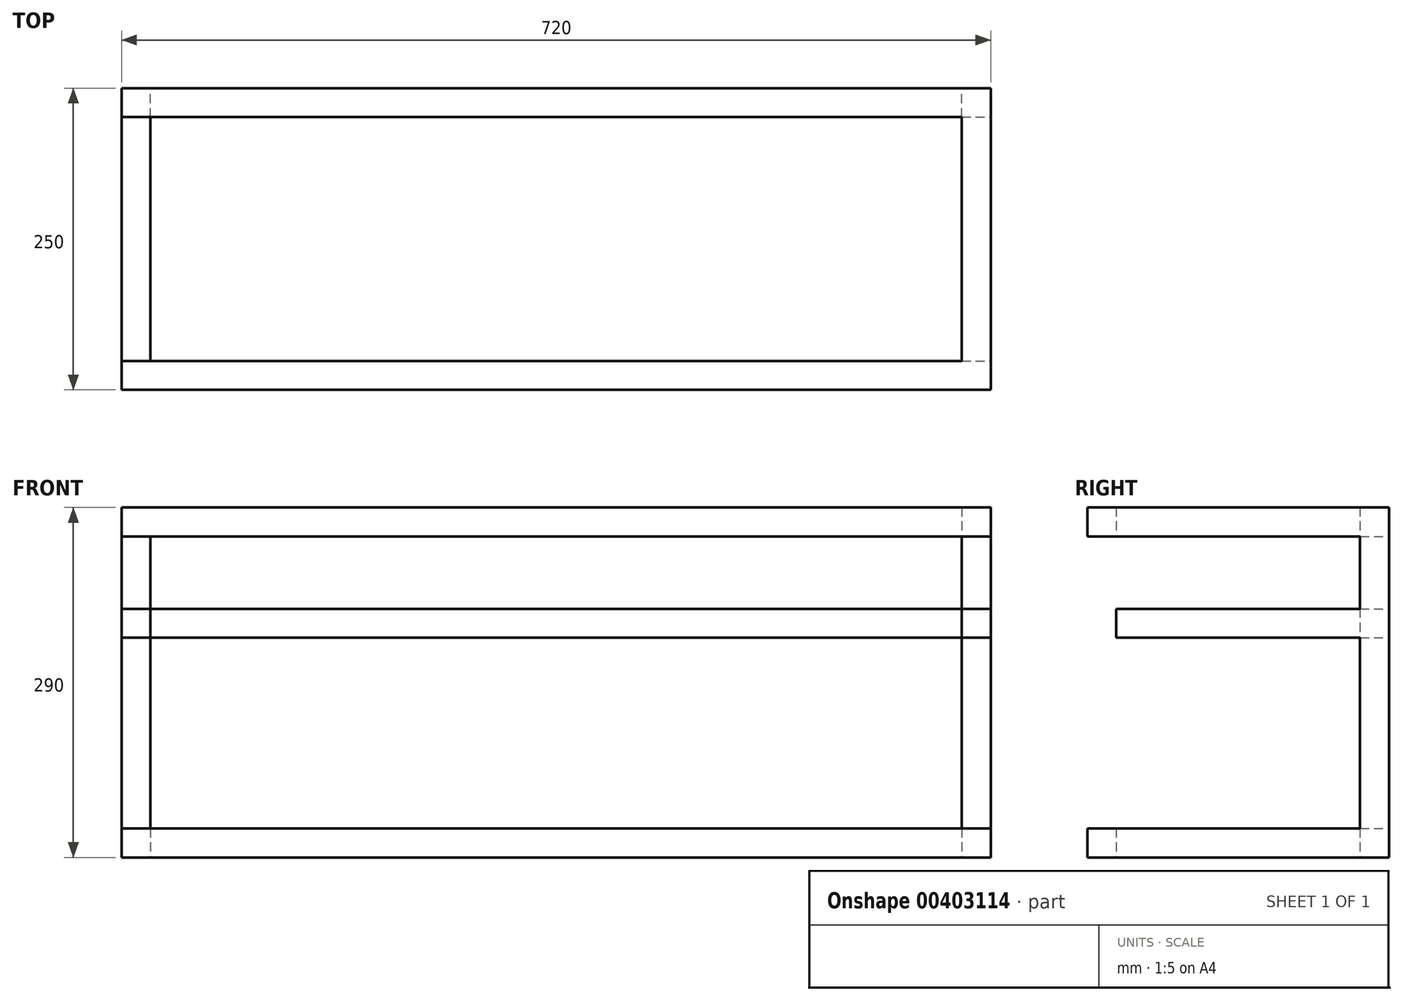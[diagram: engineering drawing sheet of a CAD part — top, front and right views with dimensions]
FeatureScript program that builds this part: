
annotation { "Feature Type Name" : "Feature", "Feature Type Description" : "" }
export const myFeature = defineFeature(function(context is Context, id is Id, definition is map)
    precondition{}
    {
        {
            var Q0;
            Q0=qCreatedBy(makeId("Front.planeOp"),FACE);
            var sketch = newSketch(context, id + "F0", { "sketchPlane" : qUnion([Q0])});
            skLineSegment(sketch, "E0.bottom", {"start": v(-354.03, 182.25) * mm, "end": v(365.97, 182.25) * mm});
            skLineSegment(sketch, "E0.top", {"start": v(-354.03, -107.75) * mm, "end": v(365.97, -107.75) * mm});
            skLineSegment(sketch, "E0.left", {"start": v(-354.03, 182.25) * mm, "end": v(-354.03, -107.75) * mm});
            skLineSegment(sketch, "E0.right", {"start": v(365.97, 182.25) * mm, "end": v(365.97, -107.75) * mm});
            skLineSegment(sketch, "E1", {"start": v(-354.03, -107.75) * mm, "end": v(-354.03, 86.25) * mm});
            skLineSegment(sketch, "E2.top", {"start": v(-354.03, 158.25) * mm, "end": v(365.97, 158.25) * mm});
            skLineSegment(sketch, "E2.left", {"start": v(-354.03, 182.25) * mm, "end": v(-354.03, 158.25) * mm});
            skLineSegment(sketch, "E2.right", {"start": v(365.97, 182.25) * mm, "end": v(365.97, 158.25) * mm});
            skLineSegment(sketch, "E3.bottom", {"start": v(365.97, 158.25) * mm, "end": v(341.97, 158.25) * mm});
            skLineSegment(sketch, "E3.left", {"start": v(365.97, 158.25) * mm, "end": v(365.97, 110.25) * mm});
            skLineSegment(sketch, "E4.bottom", {"start": v(-354.03, 158.25) * mm, "end": v(-330.03, 158.25) * mm});
            skLineSegment(sketch, "E4.left", {"start": v(-354.03, 158.25) * mm, "end": v(-354.03, 110.25) * mm});
            skLineSegment(sketch, "E5.top", {"start": v(-354.03, -83.75) * mm, "end": v(365.97, -83.75) * mm});
            skLineSegment(sketch, "E5.left", {"start": v(-354.03, -107.75) * mm, "end": v(-354.03, -83.75) * mm});
            skLineSegment(sketch, "E5.right", {"start": v(365.97, -107.75) * mm, "end": v(365.97, -83.75) * mm});
            skLineSegment(sketch, "E6.top", {"start": v(-354.03, -83.75) * mm, "end": v(-330.03, -83.75) * mm});
            skLineSegment(sketch, "E6.left", {"start": v(-354.03, 62.25) * mm, "end": v(-354.03, -83.75) * mm});
            skLineSegment(sketch, "E7.top", {"start": v(-354.03, 74.25) * mm, "end": v(365.97, 74.25) * mm});
            skLineSegment(sketch, "E7.right", {"start": v(365.97, 86.25) * mm, "end": v(365.97, 74.25) * mm});
            skLineSegment(sketch, "E8.top", {"start": v(-353.78, 98.25) * mm, "end": v(366.22, 98.25) * mm});
            skLineSegment(sketch, "E8.right", {"start": v(366.22, 86.25) * mm, "end": v(366.22, 98.25) * mm});
            skLineSegment(sketch, "E9.top", {"start": v(-353.78, 98.25) * mm, "end": v(-330.03, 98.25) * mm});
            skLineSegment(sketch, "E9.right", {"start": v(-330.03, 158.25) * mm, "end": v(-330.03, 98.25) * mm});
            skLineSegment(sketch, "E10", {"start": v(341.97, 158.25) * mm, "end": v(341.97, 98.25) * mm});
            skLineSegment(sketch, "E11", {"start": v(-330.03, -83.75) * mm, "end": v(-330.03, 74.25) * mm});
            skLineSegment(sketch, "E12", {"start": v(365.97, -83.75) * mm, "end": v(341.97, -83.75) * mm});
            skLineSegment(sketch, "E13", {"start": v(341.97, -83.75) * mm, "end": v(341.97, 74.25) * mm});
            skLineSegment(sketch, "E14", {"start": v(-354.03, 86.25) * mm, "end": v(365.97, 86.25) * mm});
            skSolve(sketch);
        }
        {
            var Q0;
            {var subQ1=sQuery(id+"F0.wireOp",EDGE,"E4.left");Q0=makeQuery(id+"F0.imprint","IMPRINT",FACE,{"disambiguationData":[TD([[makeQuery(id+"F0.imprint","IMPRINT",EDGE,{"derivedFrom":subQ1}),1.0]])]});}
            var Q1;
            Q1=makeQuery(id+"F0.imprint","IMPRINT",FACE,{"disambiguationData":[TD([[makeQuery(id+"F0.imprint","IMPRINT",EDGE,{"derivedFrom":sQuery(id+"F0.wireOp",EDGE,"E3.bottom")}),1.0]])]});
            var Q2;
            Q2=makeQuery(id+"F0.imprint","IMPRINT",FACE,{"disambiguationData":[TD([[makeQuery(id+"F0.imprint","IMPRINT",EDGE,{"derivedFrom":sQuery(id+"F0.wireOp",EDGE,"E6.top")}),1.0]])]});
            var Q3;
            {var subQ0=sQuery(id+"F0.wireOp",EDGE,"E12");Q3=makeQuery(id+"F0.imprint","IMPRINT",FACE,{"disambiguationData":[TD([[makeQuery(id+"F0.imprint","IMPRINT",EDGE,{"derivedFrom":subQ0}),-1.0]])]});}
            var Q4;
            {var subQ0=sQuery(id+"F0.wireOp",EDGE,"E7.right");Q4=makeQuery(id+"F0.imprint","IMPRINT",FACE,{"disambiguationData":[TD([[makeQuery(id+"F0.imprint","IMPRINT",EDGE,{"derivedFrom":subQ0}),-1.0]])]});}
            var Q5;
            {var subQ0=sQuery(id+"F0.wireOp",EDGE,"E8.right");Q5=makeQuery(id+"F0.imprint","IMPRINT",FACE,{"disambiguationData":[TD([[makeQuery(id+"F0.imprint","IMPRINT",EDGE,{"derivedFrom":subQ0}),1.0]])]});}
            var Q6;
            Q6=makeQuery(id+"F0.imprint","IMPRINT",FACE,{"disambiguationData":[TD([[makeQuery(id+"F0.imprint","IMPRINT",EDGE,{"derivedFrom":sQuery(id+"F0.wireOp",EDGE,"E0.bottom")}),-1.0]])]});
            var Q7;
            Q7=makeQuery(id+"F0.imprint","IMPRINT",FACE,{"disambiguationData":[TD([[makeQuery(id+"F0.imprint","IMPRINT",EDGE,{"derivedFrom":sQuery(id+"F0.wireOp",EDGE,"E0.top")}),1.0]])]});
            extrude(context, id + "F1", {"entities" : qUnion([Q0, Q1, Q2, Q3, Q4, Q5, Q6, Q7]), "oppositeDirection" : true, "depth" : 24 * mm});
        }
        {
            var Q0;
            Q0=makeQuery(id+"F1.opExtrude","CAP_FACE",FACE,{"disambiguationData":[OSD([sQuery(id+"F0.wireOp",EDGE,"E0.left"),sQuery(id+"F0.wireOp",EDGE,"E0.right"),sQuery(id+"F0.wireOp",EDGE,"E1"),sQuery(id+"F0.wireOp",EDGE,"E0.bottom"),sQuery(id+"F0.wireOp",EDGE,"E2.top"),sQuery(id+"F0.wireOp",EDGE,"E2.left"),sQuery(id+"F0.wireOp",EDGE,"E2.right"),sQuery(id+"F0.wireOp",EDGE,"E3.left"),sQuery(id+"F0.wireOp",EDGE,"E4.bottom"),sQuery(id+"F0.wireOp",EDGE,"E4.left"),sQuery(id+"F0.wireOp",EDGE,"E0.top"),sQuery(id+"F0.wireOp",EDGE,"E5.top"),sQuery(id+"F0.wireOp",EDGE,"E5.left"),sQuery(id+"F0.wireOp",EDGE,"E5.right"),sQuery(id+"F0.wireOp",EDGE,"E6.left"),sQuery(id+"F0.wireOp",EDGE,"E7.top"),sQuery(id+"F0.wireOp",EDGE,"E7.right"),sQuery(id+"F0.wireOp",EDGE,"E8.top"),sQuery(id+"F0.wireOp",EDGE,"E8.right"),sQuery(id+"F0.wireOp",EDGE,"E9.right"),sQuery(id+"F0.wireOp",EDGE,"E10"),sQuery(id+"F0.wireOp",EDGE,"E11"),sQuery(id+"F0.wireOp",EDGE,"E13")])],"isStart":false});
            var sketch = newSketch(context, id + "F2", { "sketchPlane" : qUnion([Q0])});
            skLineSegment(sketch, "E15.bottom", {"start": v(-365.97, 182.25) * mm, "end": v(-341.97, 182.25) * mm});
            skLineSegment(sketch, "E15.top", {"start": v(-365.97, 158.25) * mm, "end": v(-341.97, 158.25) * mm});
            skLineSegment(sketch, "E15.left", {"start": v(-365.97, 182.25) * mm, "end": v(-365.97, 158.25) * mm});
            skLineSegment(sketch, "E15.right", {"start": v(-341.97, 182.25) * mm, "end": v(-341.97, 158.25) * mm});
            skLineSegment(sketch, "E16.bottom", {"start": v(-341.97, 98.25) * mm, "end": v(-365.97, 98.25) * mm});
            skLineSegment(sketch, "E16.top", {"start": v(-341.97, 74.25) * mm, "end": v(-365.97, 74.25) * mm});
            skLineSegment(sketch, "E16.left", {"start": v(-341.97, 98.25) * mm, "end": v(-341.97, 74.25) * mm});
            skLineSegment(sketch, "E16.right", {"start": v(-365.97, 98.25) * mm, "end": v(-365.97, 74.25) * mm});
            skLineSegment(sketch, "E17.bottom", {"start": v(-341.97, -83.75) * mm, "end": v(-365.97, -83.75) * mm});
            skLineSegment(sketch, "E17.top", {"start": v(-341.97, -107.75) * mm, "end": v(-365.97, -107.75) * mm});
            skLineSegment(sketch, "E17.left", {"start": v(-341.97, -83.75) * mm, "end": v(-341.97, -107.75) * mm});
            skLineSegment(sketch, "E17.right", {"start": v(-365.97, -83.75) * mm, "end": v(-365.97, -107.75) * mm});
            skLineSegment(sketch, "E18.bottom", {"start": v(330.03, 158.25) * mm, "end": v(354.03, 158.25) * mm});
            skLineSegment(sketch, "E18.top", {"start": v(330.03, 182.25) * mm, "end": v(354.03, 182.25) * mm});
            skLineSegment(sketch, "E18.left", {"start": v(330.03, 158.25) * mm, "end": v(330.03, 182.25) * mm});
            skLineSegment(sketch, "E18.right", {"start": v(354.03, 158.25) * mm, "end": v(354.03, 182.25) * mm});
            skLineSegment(sketch, "E19.bottom", {"start": v(330.03, 98.25) * mm, "end": v(354.03, 98.25) * mm});
            skLineSegment(sketch, "E19.top", {"start": v(330.03, 74.25) * mm, "end": v(354.03, 74.25) * mm});
            skLineSegment(sketch, "E19.left", {"start": v(330.03, 98.25) * mm, "end": v(330.03, 74.25) * mm});
            skLineSegment(sketch, "E19.right", {"start": v(354.03, 98.25) * mm, "end": v(354.03, 74.25) * mm});
            skLineSegment(sketch, "E20.bottom", {"start": v(330.03, -83.75) * mm, "end": v(354.03, -83.75) * mm});
            skLineSegment(sketch, "E20.top", {"start": v(330.03, -107.75) * mm, "end": v(354.03, -107.75) * mm});
            skLineSegment(sketch, "E20.left", {"start": v(330.03, -83.75) * mm, "end": v(330.03, -107.75) * mm});
            skLineSegment(sketch, "E20.right", {"start": v(354.03, -83.75) * mm, "end": v(354.03, -107.75) * mm});
            skSolve(sketch);
        }
        {
            var Q0;
            Q0=makeQuery(id+"F2.imprint","IMPRINT",FACE,{"disambiguationData":[TD([[makeQuery(id+"F2.imprint","IMPRINT",EDGE,{"derivedFrom":sQuery(id+"F2.wireOp",EDGE,"E16.bottom")}),1.0]])]});
            var Q1;
            Q1=makeQuery(id+"F2.imprint","IMPRINT",FACE,{"disambiguationData":[TD([[makeQuery(id+"F2.imprint","IMPRINT",EDGE,{"derivedFrom":sQuery(id+"F2.wireOp",EDGE,"E17.bottom")}),1.0]])]});
            var Q2;
            Q2=makeQuery(id+"F2.imprint","IMPRINT",FACE,{"disambiguationData":[TD([[makeQuery(id+"F2.imprint","IMPRINT",EDGE,{"derivedFrom":sQuery(id+"F2.wireOp",EDGE,"E18.bottom")}),1.0]])]});
            var Q3;
            Q3=makeQuery(id+"F2.imprint","IMPRINT",FACE,{"disambiguationData":[TD([[makeQuery(id+"F2.imprint","IMPRINT",EDGE,{"derivedFrom":sQuery(id+"F2.wireOp",EDGE,"E20.bottom")}),-1.0]])]});
            var Q4;
            Q4=makeQuery(id+"F2.imprint","IMPRINT",FACE,{"disambiguationData":[TD([[makeQuery(id+"F2.imprint","IMPRINT",EDGE,{"derivedFrom":sQuery(id+"F2.wireOp",EDGE,"E19.bottom")}),-1.0]])]});
            var Q5;
            Q5=makeQuery(id+"F2.imprint","IMPRINT",FACE,{"disambiguationData":[TD([[makeQuery(id+"F2.imprint","IMPRINT",EDGE,{"derivedFrom":sQuery(id+"F2.wireOp",EDGE,"E15.bottom")}),1.0]])]});
            extrude(context, id + "F3", {"entities" : qUnion([Q0, Q1, Q2, Q3, Q4, Q5]), "operationType" : NewBodyOperationType.ADD, "depth" : 202 * mm});
        }
        {
            var Q0;
            Q0=makeQuery(id+"F3.boolean.opBoolean","MERGE",FACE,{"derivedFrom":[makeQuery(id+"F1.opExtrude","SWEPT_FACE",FACE,{"disambiguationData":[OSD([sQuery(id+"F0.wireOp",EDGE,"E0.right"),sQuery(id+"F0.wireOp",EDGE,"E2.right"),sQuery(id+"F0.wireOp",EDGE,"E3.left"),sQuery(id+"F0.wireOp",EDGE,"E5.right"),sQuery(id+"F0.wireOp",EDGE,"E7.right")])]}),makeQuery(id+"F3.opExtrude","SWEPT_FACE",FACE,{"disambiguationData":[OSD([sQuery(id+"F2.wireOp",EDGE,"E15.left")])]}),makeQuery(id+"F3.opExtrude","SWEPT_FACE",FACE,{"disambiguationData":[OSD([sQuery(id+"F2.wireOp",EDGE,"E16.right")])]}),makeQuery(id+"F3.opExtrude","SWEPT_FACE",FACE,{"disambiguationData":[OSD([sQuery(id+"F2.wireOp",EDGE,"E17.right")])]})]});
            var sketch = newSketch(context, id + "F4", { "sketchPlane" : qUnion([Q0])});
            skLineSegment(sketch, "E21.bottom", {"start": v(226, 182.25) * mm, "end": v(250, 182.25) * mm});
            skLineSegment(sketch, "E21.top", {"start": v(226, 158.25) * mm, "end": v(250, 158.25) * mm});
            skLineSegment(sketch, "E21.left", {"start": v(226, 182.25) * mm, "end": v(226, 158.25) * mm});
            skLineSegment(sketch, "E21.right", {"start": v(250, 182.25) * mm, "end": v(250, 158.25) * mm});
            skLineSegment(sketch, "E22.bottom", {"start": v(226, 98.25) * mm, "end": v(250, 98.25) * mm});
            skLineSegment(sketch, "E22.top", {"start": v(226, 74.25) * mm, "end": v(250, 74.25) * mm});
            skLineSegment(sketch, "E22.left", {"start": v(226, 98.25) * mm, "end": v(226, 74.25) * mm});
            skLineSegment(sketch, "E22.right", {"start": v(250, 98.25) * mm, "end": v(250, 74.25) * mm});
            skLineSegment(sketch, "E23.bottom", {"start": v(226, -83.75) * mm, "end": v(250, -83.75) * mm});
            skLineSegment(sketch, "E23.top", {"start": v(226, -107.75) * mm, "end": v(250, -107.75) * mm});
            skLineSegment(sketch, "E23.left", {"start": v(226, -83.75) * mm, "end": v(226, -107.75) * mm});
            skLineSegment(sketch, "E23.right", {"start": v(250, -83.75) * mm, "end": v(250, -107.75) * mm});
            skSolve(sketch);
        }
        {
            var Q0;
            Q0=makeQuery(id+"F4.imprint","IMPRINT",FACE,{"disambiguationData":[TD([[makeQuery(id+"F4.imprint","IMPRINT",EDGE,{"derivedFrom":sQuery(id+"F4.wireOp",EDGE,"E22.bottom")}),-1.0]])]});
            var Q1;
            Q1=makeQuery(id+"F4.imprint","IMPRINT",FACE,{"disambiguationData":[TD([[makeQuery(id+"F4.imprint","IMPRINT",EDGE,{"derivedFrom":sQuery(id+"F4.wireOp",EDGE,"E21.bottom")}),-1.0]])]});
            var Q2;
            Q2=makeQuery(id+"F4.imprint","IMPRINT",FACE,{"disambiguationData":[TD([[makeQuery(id+"F4.imprint","IMPRINT",EDGE,{"derivedFrom":sQuery(id+"F4.wireOp",EDGE,"E23.bottom")}),-1.0]])]});
            extrude(context, id + "F5", {"entities" : qUnion([Q0, Q1, Q2]), "operationType" : NewBodyOperationType.ADD, "oppositeDirection" : true, "depth" : 720 * mm});
        }
        {
            var Q0;
            Q0=makeQuery(id+"F5.boolean.opBoolean","MERGE",FACE,{"derivedFrom":[makeQuery(id+"F3.boolean.opBoolean","MERGE",FACE,{"derivedFrom":[makeQuery(id+"F1.opExtrude","SWEPT_FACE",FACE,{"disambiguationData":[OSD([sQuery(id+"F0.wireOp",EDGE,"E0.bottom")])]}),makeQuery(id+"F3.opExtrude","SWEPT_FACE",FACE,{"disambiguationData":[OSD([sQuery(id+"F2.wireOp",EDGE,"E15.bottom")])]}),makeQuery(id+"F3.opExtrude","SWEPT_FACE",FACE,{"disambiguationData":[OSD([sQuery(id+"F2.wireOp",EDGE,"E18.top")])]})]}),makeQuery(id+"F5.opExtrude","SWEPT_FACE",FACE,{"disambiguationData":[OSD([sQuery(id+"F4.wireOp",EDGE,"E21.bottom")])]})]});
            var sketch = newSketch(context, id + "F6", { "sketchPlane" : qUnion([Q0])});
            skLineSegment(sketch, "E24.bottom", {"start": v(-354.03, 250) * mm, "end": v(-330.03, 250) * mm});
            skLineSegment(sketch, "E24.top", {"start": v(-354.03, 226) * mm, "end": v(-330.03, 226) * mm});
            skLineSegment(sketch, "E24.left", {"start": v(-354.03, 250) * mm, "end": v(-354.03, 226) * mm});
            skLineSegment(sketch, "E24.right", {"start": v(-330.03, 250) * mm, "end": v(-330.03, 226) * mm});
            skLineSegment(sketch, "E25.bottom", {"start": v(365.97, 250) * mm, "end": v(341.97, 250) * mm});
            skLineSegment(sketch, "E25.top", {"start": v(365.97, 226) * mm, "end": v(341.97, 226) * mm});
            skLineSegment(sketch, "E25.left", {"start": v(365.97, 250) * mm, "end": v(365.97, 226) * mm});
            skLineSegment(sketch, "E25.right", {"start": v(341.97, 250) * mm, "end": v(341.97, 226) * mm});
            skSolve(sketch);
        }
        {
            var Q0;
            Q0=qSketchRegion(id+"F6",true);
            extrude(context, id + "F7", {"entities" : qUnion([Q0]), "operationType" : NewBodyOperationType.ADD, "oppositeDirection" : true, "depth" : 280 * mm});
        }
    });
